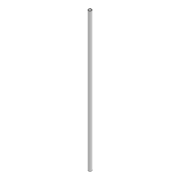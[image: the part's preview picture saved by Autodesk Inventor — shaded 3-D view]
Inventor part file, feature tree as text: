
AUTODESK INVENTOR PART (.ipt)
format: ipt  version: 2022 (Build 260153000, 153)  size: 77,824 bytes
history: native  units: mm
features: extrude x1, sketch x1
ambient origin geometry x8: Origin, YZ Plane, XZ Plane, XY Plane, X Axis, Y Axis, Z Axis, Center Point
bodies: Solid1 (feature_tree)
feature tree (2):
  extrude  "Extrusion1"  Depth=10.0mm
  sketch  "Sketch1"  dims[d0=12.0mm d1=10.0mm d2=500.0mm d3=0.0mm]
